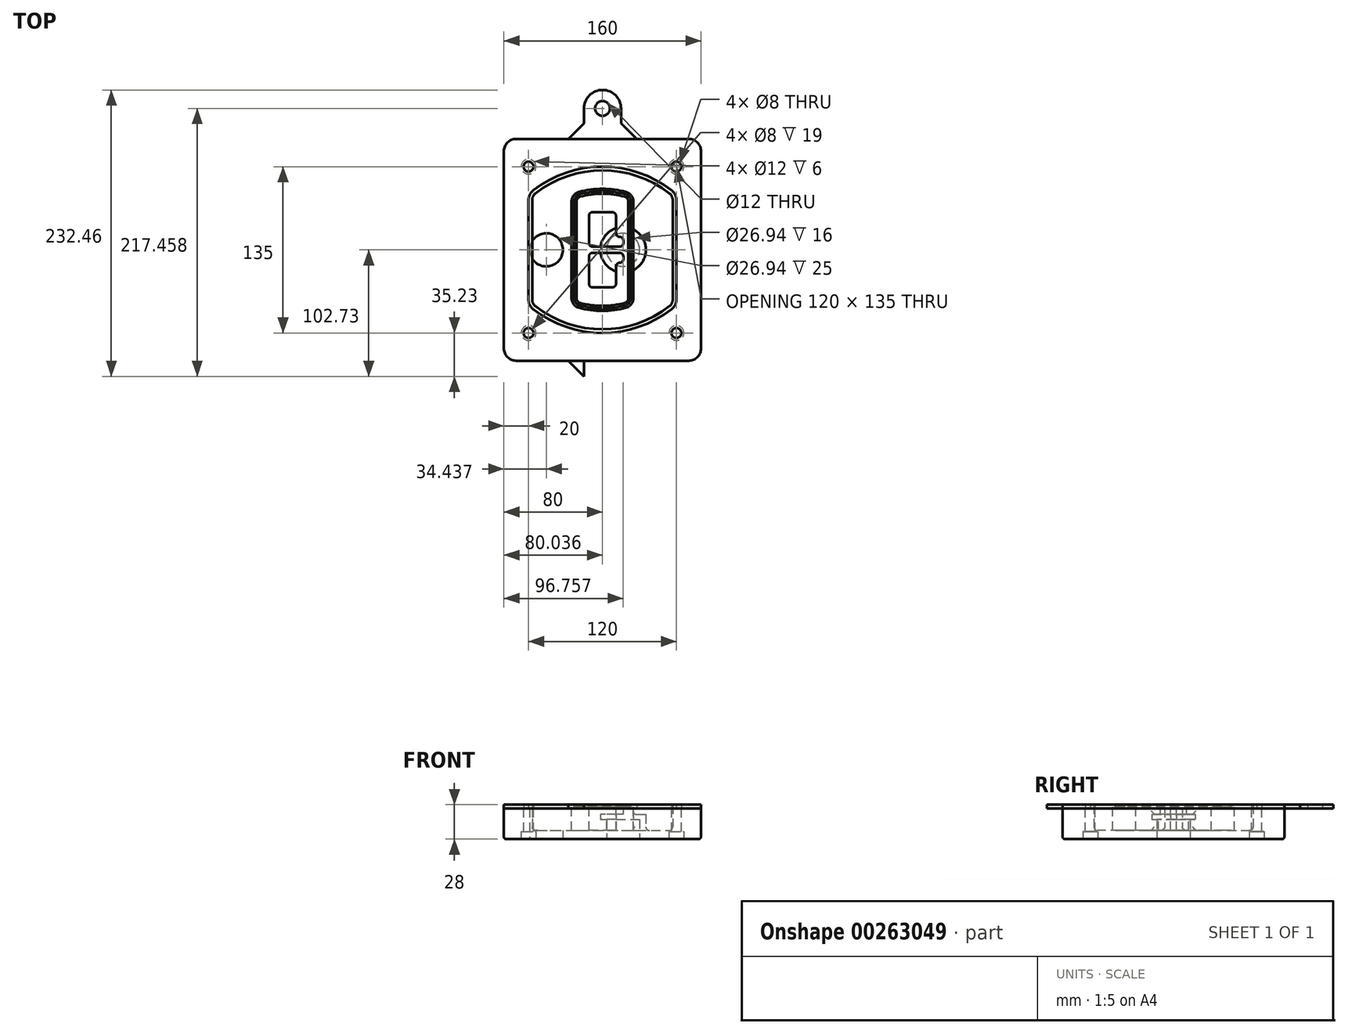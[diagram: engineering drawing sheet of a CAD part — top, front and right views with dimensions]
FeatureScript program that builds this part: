
annotation { "Feature Type Name" : "Feature", "Feature Type Description" : "" }
export const myFeature = defineFeature(function(context is Context, id is Id, definition is map)
    precondition{}
    {
        {
            var Q0;
            Q0=qCreatedBy(makeId("Top.planeOp"),FACE);
            var sketch = newSketch(context, id + "F0", { "sketchPlane" : qUnion([Q0])});
            skPoint(sketch, "E0.rect.middle", {"position": v(0, 0) * mm});
            skLineSegment(sketch, "E1.bottom", {"start": v(-70, -90) * mm, "end": v(70, -90) * mm});
            skLineSegment(sketch, "E1.top", {"start": v(-70, 90) * mm, "end": v(70, 90) * mm});
            skLineSegment(sketch, "E1.left", {"start": v(-80, -80) * mm, "end": v(-80, 80) * mm});
            skLineSegment(sketch, "E1.right", {"start": v(80, -80) * mm, "end": v(80, 80) * mm});
            skLineSegment(sketch, "E2", {"start": v(-80, 90) * mm, "end": v(80, -90) * mm, "construction": true});
            skLineSegment(sketch, "E3", {"start": v(80, 90) * mm, "end": v(-80, -90) * mm, "construction": true});
            skCircle(sketch, "E4", {"center": v(-60, 67.5) * mm, "radius": 4 * mm});
            skCircle(sketch, "E5", {"center": v(60, 67.5) * mm, "radius": 4 * mm});
            skCircle(sketch, "E6", {"center": v(60, -67.5) * mm, "radius": 4 * mm});
            skCircle(sketch, "E7", {"center": v(-60, -67.5) * mm, "radius": 4 * mm});
            skLineSegment(sketch, "E8", {"start": v(-60, 67.5) * mm, "end": v(60, 67.5) * mm, "construction": true});
            skLineSegment(sketch, "E9", {"start": v(60, 67.5) * mm, "end": v(60, -67.5) * mm, "construction": true});
            skLineSegment(sketch, "E10", {"start": v(60, -67.5) * mm, "end": v(-60, -67.5) * mm, "construction": true});
            skLineSegment(sketch, "E11", {"start": v(-60, -67.5) * mm, "end": v(-60, 67.5) * mm, "construction": true});
            skLineSegment(sketch, "E12", {"start": v(-60, 40.3) * mm, "end": v(-60, -40.3) * mm});
            skLineSegment(sketch, "E13", {"start": v(60, 40.3) * mm, "end": v(60, -40.3) * mm});
            skArc(sketch, "E14", {"start": v(56.15, 48.18) * mm, "mid": v(0, 67.5) * mm, "end": v(-56.15, 48.18) * mm});
            skArc(sketch, "E15", {"start": v(-56.15, -48.18) * mm, "mid": v(0, -67.5) * mm, "end": v(56.15, -48.18) * mm});
            skLineSegment(sketch, "E16", {"start": v(-60, 0) * mm, "end": v(60, 0) * mm, "construction": true});
            skPoint(sketch, "E17.visualSharp", {"position": v(-60, -45) * mm});
            skArc(sketch, "E17.filletArc", {"start": v(-60, -40.3) * mm, "mid": v(-58.99, -44.68) * mm, "end": v(-56.15, -48.18) * mm});
            skPoint(sketch, "E18.visualSharp", {"position": v(-60, 45) * mm});
            skArc(sketch, "E18.filletArc", {"start": v(-56.15, 48.18) * mm, "mid": v(-58.99, 44.68) * mm, "end": v(-60, 40.3) * mm});
            skPoint(sketch, "E19.visualSharp", {"position": v(60, 45) * mm});
            skArc(sketch, "E19.filletArc", {"start": v(60, 40.3) * mm, "mid": v(58.99, 44.68) * mm, "end": v(56.15, 48.18) * mm});
            skPoint(sketch, "E20.visualSharp", {"position": v(60, -45) * mm});
            skArc(sketch, "E20.filletArc", {"start": v(56.15, -48.18) * mm, "mid": v(58.99, -44.68) * mm, "end": v(60, -40.3) * mm});
            skPoint(sketch, "E21.visualSharp", {"position": v(-80, 90) * mm});
            skArc(sketch, "E21.filletArc", {"start": v(-70, 90) * mm, "mid": v(-77.07, 87.07) * mm, "end": v(-80, 80) * mm});
            skPoint(sketch, "E22.visualSharp", {"position": v(80, 90) * mm});
            skArc(sketch, "E22.filletArc", {"start": v(80, 80) * mm, "mid": v(77.07, 87.07) * mm, "end": v(70, 90) * mm});
            skPoint(sketch, "E23.visualSharp", {"position": v(80, -90) * mm});
            skArc(sketch, "E23.filletArc", {"start": v(70, -90) * mm, "mid": v(77.07, -87.07) * mm, "end": v(80, -80) * mm});
            skPoint(sketch, "E24.visualSharp", {"position": v(-80, -90) * mm});
            skArc(sketch, "E24.filletArc", {"start": v(-80, -80) * mm, "mid": v(-77.07, -87.07) * mm, "end": v(-70, -90) * mm});
            skArc(sketch, "E25.0", {"start": v(57, 40.3) * mm, "mid": v(56.3, 43.36) * mm, "end": v(54.3, 45.81) * mm});
            skLineSegment(sketch, "E25.1", {"start": v(57, 40.3) * mm, "end": v(57, -40.3) * mm});
            skArc(sketch, "E25.2", {"start": v(54.3, -45.81) * mm, "mid": v(56.3, -43.36) * mm, "end": v(57, -40.3) * mm});
            skArc(sketch, "E25.3", {"start": v(-54.3, -45.81) * mm, "mid": v(0, -64.5) * mm, "end": v(54.3, -45.81) * mm});
            skArc(sketch, "E25.4", {"start": v(-57, -40.3) * mm, "mid": v(-56.3, -43.36) * mm, "end": v(-54.3, -45.81) * mm});
            skArc(sketch, "E25.5", {"start": v(54.3, 45.81) * mm, "mid": v(0, 64.5) * mm, "end": v(-54.3, 45.81) * mm});
            skLineSegment(sketch, "E25.6", {"start": v(-57, 40.3) * mm, "end": v(-57, -40.3) * mm});
            skArc(sketch, "E25.7", {"start": v(-54.3, 45.81) * mm, "mid": v(-56.3, 43.36) * mm, "end": v(-57, 40.3) * mm});
            skArc(sketch, "E26.0", {"start": v(-58.62, 51.33) * mm, "mid": v(-62.58, 46.43) * mm, "end": v(-64, 40.3) * mm});
            skArc(sketch, "E26.1", {"start": v(58.62, 51.33) * mm, "mid": v(0, 71.5) * mm, "end": v(-58.62, 51.33) * mm});
            skArc(sketch, "E26.2", {"start": v(64, 40.3) * mm, "mid": v(62.58, 46.43) * mm, "end": v(58.62, 51.33) * mm});
            skLineSegment(sketch, "E26.3", {"start": v(64, 40.3) * mm, "end": v(64, -40.3) * mm});
            skArc(sketch, "E26.4", {"start": v(58.62, -51.33) * mm, "mid": v(62.58, -46.43) * mm, "end": v(64, -40.3) * mm});
            skLineSegment(sketch, "E26.5", {"start": v(-64, 40.3) * mm, "end": v(-64, -40.3) * mm});
            skArc(sketch, "E26.6", {"start": v(-58.62, -51.33) * mm, "mid": v(0, -71.5) * mm, "end": v(58.62, -51.33) * mm});
            skArc(sketch, "E26.7", {"start": v(-64, -40.3) * mm, "mid": v(-62.58, -46.43) * mm, "end": v(-58.62, -51.33) * mm});
            skSolve(sketch);
        }
        {
            var Q0;
            Q0=makeQuery(id+"F0.imprint","IMPRINT",FACE,{"disambiguationData":[TD([[makeQuery(id+"F0.imprint","IMPRINT",EDGE,{"derivedFrom":sQuery(id+"F0.wireOp",EDGE,"E1.bottom")}),1.0]])]});
            var Q1;
            Q1=makeQuery(id+"F0.imprint","IMPRINT",FACE,{"disambiguationData":[TD([[makeQuery(id+"F0.imprint","IMPRINT",EDGE,{"derivedFrom":sQuery(id+"F0.wireOp",EDGE,"E12")}),1.0]])]});
            var Q2;
            Q2=makeQuery(id+"F0.imprint","IMPRINT",FACE,{"disambiguationData":[TD([[makeQuery(id+"F0.imprint","IMPRINT",EDGE,{"derivedFrom":sQuery(id+"F0.wireOp",EDGE,"E25.0")}),1.0]])]});
            var Q3;
            Q3=makeQuery(id+"F0.imprint","IMPRINT",FACE,{"disambiguationData":[TD([[makeQuery(id+"F0.imprint","IMPRINT",EDGE,{"derivedFrom":sQuery(id+"F0.wireOp",EDGE,"E12")}),-1.0]])]});
            extrude(context, id + "F1", {"entities" : qUnion([Q0, Q1, Q2, Q3]), "oppositeDirection" : true, "depth" : 25 * mm});
        }
        {
            var Q0;
            Q0=makeQuery(id+"F0.imprint","IMPRINT",FACE,{"disambiguationData":[TD([[makeQuery(id+"F0.imprint","IMPRINT",EDGE,{"derivedFrom":sQuery(id+"F0.wireOp",EDGE,"E12")}),1.0]])]});
            extrude(context, id + "F2", {"entities" : qUnion([Q0]), "operationType" : NewBodyOperationType.ADD, "depth" : 3 * mm});
        }
        {
            var Q0;
            Q0=makeQuery(id+"F0.imprint","IMPRINT",FACE,{"disambiguationData":[TD([[makeQuery(id+"F0.imprint","IMPRINT",EDGE,{"derivedFrom":sQuery(id+"F0.wireOp",EDGE,"E25.0")}),1.0]])]});
            extrude(context, id + "F3", {"entities" : qUnion([Q0]), "operationType" : NewBodyOperationType.REMOVE, "oppositeDirection" : true, "depth" : 18 * mm});
        }
        {
            var Q0;
            Q0=makeQuery(id+"F2.opExtrude","CAP_FACE",FACE,{"disambiguationData":[OSD([sQuery(id+"F0.wireOp",EDGE,"E12"),sQuery(id+"F0.wireOp",EDGE,"E13"),sQuery(id+"F0.wireOp",EDGE,"E14"),sQuery(id+"F0.wireOp",EDGE,"E15"),sQuery(id+"F0.wireOp",EDGE,"E17.filletArc"),sQuery(id+"F0.wireOp",EDGE,"E18.filletArc"),sQuery(id+"F0.wireOp",EDGE,"E19.filletArc"),sQuery(id+"F0.wireOp",EDGE,"E20.filletArc"),sQuery(id+"F0.wireOp",EDGE,"E25.0"),sQuery(id+"F0.wireOp",EDGE,"E25.1"),sQuery(id+"F0.wireOp",EDGE,"E25.2"),sQuery(id+"F0.wireOp",EDGE,"E25.3"),sQuery(id+"F0.wireOp",EDGE,"E25.4"),sQuery(id+"F0.wireOp",EDGE,"E25.5"),sQuery(id+"F0.wireOp",EDGE,"E25.6"),sQuery(id+"F0.wireOp",EDGE,"E25.7")])],"isStart":false});
            var sketch = newSketch(context, id + "F4", { "sketchPlane" : qUnion([Q0])});
            skArc(sketch, "E27.0", {"start": v(-19.08, -46.97) * mm, "mid": v(0, -49.5) * mm, "end": v(19.08, -46.97) * mm});
            skArc(sketch, "E28.0", {"start": v(19.08, 46.97) * mm, "mid": v(0, 49.5) * mm, "end": v(-19.08, 46.97) * mm});
            skLineSegment(sketch, "E29", {"start": v(-25, 39.25) * mm, "end": v(-25, -39.25) * mm});
            skLineSegment(sketch, "E30", {"start": v(25, 39.25) * mm, "end": v(25, -39.25) * mm});
            skLineSegment(sketch, "E31", {"start": v(-25, 45.1) * mm, "end": v(25, 45.1) * mm, "construction": true});
            skLineSegment(sketch, "E32", {"start": v(-25, -45.1) * mm, "end": v(25, -45.1) * mm, "construction": true});
            skPoint(sketch, "E33.visualSharp", {"position": v(-25, 45.1) * mm});
            skArc(sketch, "E33.filletArc", {"start": v(-19.08, 46.97) * mm, "mid": v(-23.35, 44.11) * mm, "end": v(-25, 39.25) * mm});
            skPoint(sketch, "E34.visualSharp", {"position": v(25, 45.1) * mm});
            skArc(sketch, "E34.filletArc", {"start": v(25, 39.25) * mm, "mid": v(23.35, 44.11) * mm, "end": v(19.08, 46.97) * mm});
            skPoint(sketch, "E35.visualSharp", {"position": v(25, -45.1) * mm});
            skArc(sketch, "E35.filletArc", {"start": v(19.08, -46.97) * mm, "mid": v(23.35, -44.11) * mm, "end": v(25, -39.25) * mm});
            skPoint(sketch, "E36.visualSharp", {"position": v(-25, -45.1) * mm});
            skArc(sketch, "E36.filletArc", {"start": v(-25, -39.25) * mm, "mid": v(-23.35, -44.11) * mm, "end": v(-19.08, -46.97) * mm});
            skArc(sketch, "E37.0", {"start": v(54.3, 45.81) * mm, "mid": v(0, 64.5) * mm, "end": v(-54.3, 45.81) * mm});
            skArc(sketch, "E37.1", {"start": v(-54.3, 45.81) * mm, "mid": v(-56.3, 43.36) * mm, "end": v(-57, 40.3) * mm});
            skLineSegment(sketch, "E37.2", {"start": v(-57, 40.3) * mm, "end": v(-57, -40.3) * mm});
            skArc(sketch, "E37.3", {"start": v(-57, -40.3) * mm, "mid": v(-56.3, -43.36) * mm, "end": v(-54.3, -45.81) * mm});
            skArc(sketch, "E37.4", {"start": v(-54.3, -45.81) * mm, "mid": v(0, -64.5) * mm, "end": v(54.3, -45.81) * mm});
            skArc(sketch, "E37.5", {"start": v(54.3, -45.81) * mm, "mid": v(56.3, -43.36) * mm, "end": v(57, -40.3) * mm});
            skLineSegment(sketch, "E37.6", {"start": v(57, 40.3) * mm, "end": v(57, -40.3) * mm});
            skArc(sketch, "E37.7", {"start": v(57, 40.3) * mm, "mid": v(56.3, 43.36) * mm, "end": v(54.3, 45.81) * mm});
            skLineSegment(sketch, "E38.0", {"start": v(23, 39.25) * mm, "end": v(23, -39.25) * mm});
            skArc(sketch, "E38.1", {"start": v(18.56, -45.04) * mm, "mid": v(21.76, -42.9) * mm, "end": v(23, -39.25) * mm});
            skArc(sketch, "E38.2", {"start": v(-18.56, -45.04) * mm, "mid": v(0, -47.5) * mm, "end": v(18.56, -45.04) * mm});
            skArc(sketch, "E38.3", {"start": v(-23, -39.25) * mm, "mid": v(-21.76, -42.9) * mm, "end": v(-18.56, -45.04) * mm});
            skLineSegment(sketch, "E38.4", {"start": v(-23, 39.25) * mm, "end": v(-23, -39.25) * mm});
            skArc(sketch, "E38.5", {"start": v(23, 39.25) * mm, "mid": v(21.76, 42.9) * mm, "end": v(18.56, 45.04) * mm});
            skArc(sketch, "E38.6", {"start": v(-18.56, 45.04) * mm, "mid": v(-21.76, 42.9) * mm, "end": v(-23, 39.25) * mm});
            skArc(sketch, "E38.7", {"start": v(18.56, 45.04) * mm, "mid": v(0, 47.5) * mm, "end": v(-18.56, 45.04) * mm});
            skArc(sketch, "E39.0", {"start": v(21, 39.25) * mm, "mid": v(20.18, 41.68) * mm, "end": v(18.04, 43.1) * mm});
            skLineSegment(sketch, "E39.1", {"start": v(21, 39.25) * mm, "end": v(21, -39.25) * mm});
            skArc(sketch, "E39.2", {"start": v(18.04, -43.1) * mm, "mid": v(20.18, -41.68) * mm, "end": v(21, -39.25) * mm});
            skArc(sketch, "E39.3", {"start": v(-18.04, -43.1) * mm, "mid": v(0, -45.5) * mm, "end": v(18.04, -43.1) * mm});
            skArc(sketch, "E39.4", {"start": v(-21, -39.25) * mm, "mid": v(-20.18, -41.68) * mm, "end": v(-18.04, -43.1) * mm});
            skArc(sketch, "E39.5", {"start": v(18.04, 43.1) * mm, "mid": v(0, 45.5) * mm, "end": v(-18.04, 43.1) * mm});
            skLineSegment(sketch, "E39.6", {"start": v(-21, 39.25) * mm, "end": v(-21, -39.25) * mm});
            skArc(sketch, "E39.7", {"start": v(-18.04, 43.1) * mm, "mid": v(-20.18, 41.68) * mm, "end": v(-21, 39.25) * mm});
            skLineSegment(sketch, "E40", {"start": v(-25, 0) * mm, "end": v(25, 0) * mm, "construction": true});
            skLineSegment(sketch, "E41", {"start": v(-11, 5.5) * mm, "end": v(-11, 27.5) * mm});
            skLineSegment(sketch, "E42", {"start": v(-8, 30.5) * mm, "end": v(8, 30.5) * mm});
            skLineSegment(sketch, "E43", {"start": v(11, 27.5) * mm, "end": v(11, 13.5) * mm});
            skLineSegment(sketch, "E44", {"start": v(14, 10.5) * mm, "end": v(14, 10.5) * mm});
            skLineSegment(sketch, "E45", {"start": v(17, 7.5) * mm, "end": v(17, 5.5) * mm});
            skLineSegment(sketch, "E46", {"start": v(14, 2.5) * mm, "end": v(-8, 2.5) * mm});
            skPoint(sketch, "E47.visualSharp", {"position": v(-11, 30.5) * mm});
            skArc(sketch, "E47.filletArc", {"start": v(-8, 30.5) * mm, "mid": v(-10.12, 29.62) * mm, "end": v(-11, 27.5) * mm});
            skPoint(sketch, "E48.visualSharp", {"position": v(11, 30.5) * mm});
            skArc(sketch, "E48.filletArc", {"start": v(11, 27.5) * mm, "mid": v(10.12, 29.62) * mm, "end": v(8, 30.5) * mm});
            skPoint(sketch, "E49.visualSharp", {"position": v(11, 10.5) * mm});
            skArc(sketch, "E49.filletArc", {"start": v(11, 13.5) * mm, "mid": v(11.88, 11.38) * mm, "end": v(14, 10.5) * mm});
            skPoint(sketch, "E50.visualSharp", {"position": v(17, 10.5) * mm});
            skArc(sketch, "E50.filletArc", {"start": v(17, 7.5) * mm, "mid": v(16.12, 9.62) * mm, "end": v(14, 10.5) * mm});
            skPoint(sketch, "E51.visualSharp", {"position": v(17, 2.5) * mm});
            skArc(sketch, "E51.filletArc", {"start": v(14, 2.5) * mm, "mid": v(16.12, 3.38) * mm, "end": v(17, 5.5) * mm});
            skPoint(sketch, "E52.visualSharp", {"position": v(-11, 2.5) * mm});
            skArc(sketch, "E52.filletArc", {"start": v(-11, 5.5) * mm, "mid": v(-10.12, 3.38) * mm, "end": v(-8, 2.5) * mm});
            skLineSegment(sketch, "E53.0.MirrorCS", {"start": v(14, -2.5) * mm, "end": v(-8, -2.5) * mm});
            skArc(sketch, "E54.0.MirrorCS", {"start": v(-11, -5.5) * mm, "mid": v(-10.12, -3.38) * mm, "end": v(-8, -2.5) * mm});
            skLineSegment(sketch, "E55.0.MirrorCS", {"start": v(-11, -5.5) * mm, "end": v(-11, -27.5) * mm});
            skArc(sketch, "E56.0.MirrorCS", {"start": v(-8, -30.5) * mm, "mid": v(-10.12, -29.62) * mm, "end": v(-11, -27.5) * mm});
            skLineSegment(sketch, "E57.0.MirrorCS", {"start": v(-8, -30.5) * mm, "end": v(8, -30.5) * mm});
            skArc(sketch, "E58.0.MirrorCS", {"start": v(11, -27.5) * mm, "mid": v(10.12, -29.62) * mm, "end": v(8, -30.5) * mm});
            skLineSegment(sketch, "E59.0.MirrorCS", {"start": v(11, -27.5) * mm, "end": v(11, -13.5) * mm});
            skArc(sketch, "E60.0.MirrorCS", {"start": v(11, -13.5) * mm, "mid": v(11.88, -11.38) * mm, "end": v(14, -10.5) * mm});
            skArc(sketch, "E61.0.MirrorCS", {"start": v(17, -7.5) * mm, "mid": v(16.12, -9.62) * mm, "end": v(14, -10.5) * mm});
            skLineSegment(sketch, "E62.0.MirrorCS", {"start": v(17, -7.5) * mm, "end": v(17, -5.5) * mm});
            skArc(sketch, "E63.0.MirrorCS", {"start": v(14, -2.5) * mm, "mid": v(16.12, -3.38) * mm, "end": v(17, -5.5) * mm});
            skSolve(sketch);
        }
        {
            var Q0;
            Q0=makeQuery(id+"F4.imprint","IMPRINT",FACE,{"disambiguationData":[TD([[makeQuery(id+"F4.imprint","IMPRINT",EDGE,{"derivedFrom":sQuery(id+"F4.wireOp",EDGE,"E27.0")}),1.0]])]});
            var Q1;
            Q1=makeQuery(id+"F4.imprint","IMPRINT",FACE,{"disambiguationData":[TD([[makeQuery(id+"F4.imprint","IMPRINT",EDGE,{"derivedFrom":sQuery(id+"F4.wireOp",EDGE,"E38.0")}),-1.0]])]});
            var Q2;
            Q2=makeQuery(id+"F4.imprint","IMPRINT",FACE,{"disambiguationData":[TD([[makeQuery(id+"F4.imprint","IMPRINT",EDGE,{"derivedFrom":sQuery(id+"F4.wireOp",EDGE,"E39.0")}),1.0]])]});
            extrude(context, id + "F5", {"entities" : qUnion([Q0, Q1, Q2]), "operationType" : NewBodyOperationType.ADD, "endBound" : BoundingType.UP_TO_NEXT, "oppositeDirection" : true, "depth" : 25 * mm});
        }
        {
            var Q0;
            Q0=makeQuery(id+"F4.imprint","IMPRINT",FACE,{"disambiguationData":[TD([[makeQuery(id+"F4.imprint","IMPRINT",EDGE,{"derivedFrom":sQuery(id+"F4.wireOp",EDGE,"E38.0")}),-1.0]])]});
            extrude(context, id + "F6", {"entities" : qUnion([Q0]), "operationType" : NewBodyOperationType.REMOVE, "oppositeDirection" : true, "depth" : 2 * mm});
        }
        {
            var Q0;
            Q0=makeQuery(id+"F1.opExtrude","CAP_FACE",FACE,{"disambiguationData":[OSD([sQuery(id+"F0.wireOp",EDGE,"E1.bottom"),sQuery(id+"F0.wireOp",EDGE,"E1.top"),sQuery(id+"F0.wireOp",EDGE,"E1.left"),sQuery(id+"F0.wireOp",EDGE,"E1.right"),sQuery(id+"F0.wireOp",EDGE,"E4"),sQuery(id+"F0.wireOp",EDGE,"E5"),sQuery(id+"F0.wireOp",EDGE,"E6"),sQuery(id+"F0.wireOp",EDGE,"E7"),sQuery(id+"F0.wireOp",EDGE,"E21.filletArc"),sQuery(id+"F0.wireOp",EDGE,"E22.filletArc"),sQuery(id+"F0.wireOp",EDGE,"E23.filletArc"),sQuery(id+"F0.wireOp",EDGE,"E24.filletArc")])],"isStart":false});
            var sketch = newSketch(context, id + "F7", { "sketchPlane" : qUnion([Q0])});
            skCircle(sketch, "E64", {"center": v(16.76, 0) * mm, "radius": 13.47 * mm});
            skCircle(sketch, "E65", {"center": v(-45.56, 0) * mm, "radius": 13.47 * mm});
            skLineSegment(sketch, "E66", {"start": v(80, 0) * mm, "end": v(-80, 0) * mm});
            skCircle(sketch, "E67", {"center": v(16.76, 0) * mm, "radius": 18.47 * mm});
            skCircle(sketch, "E68", {"center": v(60, -67.5) * mm, "radius": 6 * mm});
            skCircle(sketch, "E69", {"center": v(-60, -67.5) * mm, "radius": 6 * mm});
            skCircle(sketch, "E70", {"center": v(-60, 67.5) * mm, "radius": 6 * mm});
            skCircle(sketch, "E71", {"center": v(60, 67.5) * mm, "radius": 6 * mm});
            skSolve(sketch);
        }
        {
            var Q0;
            {var subQ1=sQuery(id+"F7.wireOp",EDGE,"E66");var subQ4=sQuery(id+"F7.wireOp",EDGE,"E64");var subQ6=makeQuery(id+"F7.imprint","INTERSECT",VERTEX,{"disambiguationData":[OD(0.0)],"derivedFrom":[subQ4,subQ1]});Q0=makeQuery(id+"F7.imprint","IMPRINT",FACE,{"disambiguationData":[TD([[makeQuery(id+"F7.imprint","IMPRINT",EDGE,{"disambiguationData":[TD([[subQ6,-1.0]])],"derivedFrom":subQ4}),-1.0]])]});}
            var Q1;
            {var subQ0=sQuery(id+"F7.wireOp",EDGE,"E66");var subQ1=sQuery(id+"F7.wireOp",EDGE,"E64");var subQ3=makeQuery(id+"F7.imprint","INTERSECT",VERTEX,{"disambiguationData":[OD(0.0)],"derivedFrom":[subQ1,subQ0]});Q1=makeQuery(id+"F7.imprint","IMPRINT",FACE,{"disambiguationData":[TD([[makeQuery(id+"F7.imprint","IMPRINT",EDGE,{"disambiguationData":[TD([[subQ3,-1.0]])],"derivedFrom":subQ1}),1.0]])]});}
            var Q2;
            {var subQ0=sQuery(id+"F7.wireOp",EDGE,"E66");var subQ1=sQuery(id+"F7.wireOp",EDGE,"E64");var subQ3=makeQuery(id+"F7.imprint","INTERSECT",VERTEX,{"disambiguationData":[OD(0.0)],"derivedFrom":[subQ1,subQ0]});Q2=makeQuery(id+"F7.imprint","IMPRINT",FACE,{"disambiguationData":[TD([[makeQuery(id+"F7.imprint","IMPRINT",EDGE,{"disambiguationData":[TD([[subQ3,1.0]])],"derivedFrom":subQ1}),1.0]])]});}
            var Q3;
            {var subQ1=sQuery(id+"F7.wireOp",EDGE,"E66");var subQ4=sQuery(id+"F7.wireOp",EDGE,"E64");var subQ6=makeQuery(id+"F7.imprint","INTERSECT",VERTEX,{"disambiguationData":[OD(0.0)],"derivedFrom":[subQ4,subQ1]});Q3=makeQuery(id+"F7.imprint","IMPRINT",FACE,{"disambiguationData":[TD([[makeQuery(id+"F7.imprint","IMPRINT",EDGE,{"disambiguationData":[TD([[subQ6,1.0]])],"derivedFrom":subQ4}),-1.0]])]});}
            extrude(context, id + "F8", {"entities" : qUnion([Q0, Q1, Q2, Q3]), "operationType" : NewBodyOperationType.ADD, "oppositeDirection" : true, "depth" : 20 * mm});
        }
        {
            var Q0;
            {var subQ0=sQuery(id+"F7.wireOp",EDGE,"E66");var subQ1=sQuery(id+"F7.wireOp",EDGE,"E64");var subQ3=makeQuery(id+"F7.imprint","INTERSECT",VERTEX,{"disambiguationData":[OD(0.0)],"derivedFrom":[subQ1,subQ0]});Q0=makeQuery(id+"F7.imprint","IMPRINT",FACE,{"disambiguationData":[TD([[makeQuery(id+"F7.imprint","IMPRINT",EDGE,{"disambiguationData":[TD([[subQ3,-1.0]])],"derivedFrom":subQ1}),1.0]])]});}
            var Q1;
            {var subQ0=sQuery(id+"F7.wireOp",EDGE,"E66");var subQ1=sQuery(id+"F7.wireOp",EDGE,"E64");var subQ3=makeQuery(id+"F7.imprint","INTERSECT",VERTEX,{"disambiguationData":[OD(0.0)],"derivedFrom":[subQ1,subQ0]});Q1=makeQuery(id+"F7.imprint","IMPRINT",FACE,{"disambiguationData":[TD([[makeQuery(id+"F7.imprint","IMPRINT",EDGE,{"disambiguationData":[TD([[subQ3,1.0]])],"derivedFrom":subQ1}),1.0]])]});}
            extrude(context, id + "F9", {"entities" : qUnion([Q0, Q1]), "operationType" : NewBodyOperationType.REMOVE, "oppositeDirection" : true, "depth" : 16 * mm});
        }
        {
            var Q0;
            {var subQ0=sQuery(id+"F7.wireOp",EDGE,"E66");var subQ1=sQuery(id+"F7.wireOp",EDGE,"E65");var subQ3=makeQuery(id+"F7.imprint","INTERSECT",VERTEX,{"disambiguationData":[OD(0.0)],"derivedFrom":[subQ1,subQ0]});Q0=makeQuery(id+"F7.imprint","IMPRINT",FACE,{"disambiguationData":[TD([[makeQuery(id+"F7.imprint","IMPRINT",EDGE,{"disambiguationData":[TD([[subQ3,-1.0]])],"derivedFrom":subQ1}),1.0]])]});}
            var Q1;
            {var subQ0=sQuery(id+"F7.wireOp",EDGE,"E66");var subQ1=sQuery(id+"F7.wireOp",EDGE,"E65");var subQ3=makeQuery(id+"F7.imprint","INTERSECT",VERTEX,{"disambiguationData":[OD(0.0)],"derivedFrom":[subQ1,subQ0]});Q1=makeQuery(id+"F7.imprint","IMPRINT",FACE,{"disambiguationData":[TD([[makeQuery(id+"F7.imprint","IMPRINT",EDGE,{"disambiguationData":[TD([[subQ3,1.0]])],"derivedFrom":subQ1}),1.0]])]});}
            extrude(context, id + "F10", {"entities" : qUnion([Q0, Q1]), "operationType" : NewBodyOperationType.REMOVE, "oppositeDirection" : true, "depth" : 25 * mm});
        }
        {
            var Q0;
            Q0=makeQuery(id+"F7.imprint","IMPRINT",FACE,{"disambiguationData":[TD([[makeQuery(id+"F7.imprint","IMPRINT",EDGE,{"derivedFrom":sQuery(id+"F7.wireOp",EDGE,"E68")}),1.0]])]});
            var Q1;
            Q1=makeQuery(id+"F7.imprint","IMPRINT",FACE,{"disambiguationData":[TD([[makeQuery(id+"F7.imprint","IMPRINT",EDGE,{"derivedFrom":makeQuery(id+"F1.opExtrude","CAP_EDGE",EDGE,{"disambiguationData":[OSD([sQuery(id+"F0.wireOp",EDGE,"E5")])],"isStart":false})}),-1.0]])]});
            var Q2;
            Q2=makeQuery(id+"F7.imprint","IMPRINT",FACE,{"disambiguationData":[TD([[makeQuery(id+"F7.imprint","IMPRINT",EDGE,{"derivedFrom":sQuery(id+"F7.wireOp",EDGE,"E69")}),1.0]])]});
            var Q3;
            Q3=makeQuery(id+"F7.imprint","IMPRINT",FACE,{"disambiguationData":[TD([[makeQuery(id+"F7.imprint","IMPRINT",EDGE,{"derivedFrom":makeQuery(id+"F1.opExtrude","CAP_EDGE",EDGE,{"disambiguationData":[OSD([sQuery(id+"F0.wireOp",EDGE,"E4")])],"isStart":false})}),-1.0]])]});
            var Q4;
            Q4=makeQuery(id+"F7.imprint","IMPRINT",FACE,{"disambiguationData":[TD([[makeQuery(id+"F7.imprint","IMPRINT",EDGE,{"derivedFrom":sQuery(id+"F7.wireOp",EDGE,"E70")}),1.0]])]});
            var Q5;
            Q5=makeQuery(id+"F7.imprint","IMPRINT",FACE,{"disambiguationData":[TD([[makeQuery(id+"F7.imprint","IMPRINT",EDGE,{"derivedFrom":makeQuery(id+"F1.opExtrude","CAP_EDGE",EDGE,{"disambiguationData":[OSD([sQuery(id+"F0.wireOp",EDGE,"E7")])],"isStart":false})}),-1.0]])]});
            var Q6;
            Q6=makeQuery(id+"F7.imprint","IMPRINT",FACE,{"disambiguationData":[TD([[makeQuery(id+"F7.imprint","IMPRINT",EDGE,{"derivedFrom":sQuery(id+"F7.wireOp",EDGE,"E71")}),1.0]])]});
            var Q7;
            Q7=makeQuery(id+"F7.imprint","IMPRINT",FACE,{"disambiguationData":[TD([[makeQuery(id+"F7.imprint","IMPRINT",EDGE,{"derivedFrom":makeQuery(id+"F1.opExtrude","CAP_EDGE",EDGE,{"disambiguationData":[OSD([sQuery(id+"F0.wireOp",EDGE,"E6")])],"isStart":false})}),-1.0]])]});
            extrude(context, id + "F11", {"entities" : qUnion([Q0, Q1, Q2, Q3, Q4, Q5, Q6, Q7]), "operationType" : NewBodyOperationType.REMOVE, "oppositeDirection" : true, "depth" : 6 * mm});
        }
        {
            var Q0;
            Q0=makeQuery(id+"F9.boolean.opBoolean","COPY",FACE,{"derivedFrom":makeQuery(id+"F9.opExtrude","CAP_FACE",FACE,{"disambiguationData":[OSD([sQuery(id+"F7.wireOp",EDGE,"E64")])],"isStart":false})});
            var sketch = newSketch(context, id + "F12", { "sketchPlane" : qUnion([Q0])});
            skArc(sketch, "E72.0", {"start": v(11, 17.55) * mm, "mid": v(2.57, 11.82) * mm, "end": v(-1.54, 2.5) * mm});
            skArc(sketch, "E72.1", {"start": v(-1.54, -2.5) * mm, "mid": v(2.57, -11.82) * mm, "end": v(11, -17.55) * mm});
            skLineSegment(sketch, "E73", {"start": v(-1.54, -2.5) * mm, "end": v(14, -2.5) * mm});
            skLineSegment(sketch, "E74.0", {"start": v(14, 2.5) * mm, "end": v(-1.54, 2.5) * mm});
            skArc(sketch, "E74.1", {"start": v(14, 2.5) * mm, "mid": v(16.12, 3.38) * mm, "end": v(17, 5.5) * mm});
            skLineSegment(sketch, "E74.2", {"start": v(17, 7.5) * mm, "end": v(17, 5.5) * mm});
            skArc(sketch, "E74.3", {"start": v(17, 7.5) * mm, "mid": v(16.12, 9.62) * mm, "end": v(14, 10.5) * mm});
            skArc(sketch, "E74.4", {"start": v(11, 13.5) * mm, "mid": v(11.88, 11.38) * mm, "end": v(14, 10.5) * mm});
            skLineSegment(sketch, "E74.5", {"start": v(11, 17.55) * mm, "end": v(11, 13.5) * mm});
            skLineSegment(sketch, "E74.7", {"start": v(14, -2.5) * mm, "end": v(-1.54, -2.5) * mm});
            skArc(sketch, "E74.8", {"start": v(14, -2.5) * mm, "mid": v(16.12, -3.38) * mm, "end": v(17, -5.5) * mm});
            skLineSegment(sketch, "E74.9", {"start": v(17, -7.5) * mm, "end": v(17, -5.5) * mm});
            skArc(sketch, "E74.10", {"start": v(17, -7.5) * mm, "mid": v(16.12, -9.62) * mm, "end": v(14, -10.5) * mm});
            skArc(sketch, "E74.11", {"start": v(11, -13.5) * mm, "mid": v(11.88, -11.38) * mm, "end": v(14, -10.5) * mm});
            skLineSegment(sketch, "E74.12", {"start": v(11, -17.55) * mm, "end": v(11, -13.5) * mm});
            skPoint(sketch, "E75.orphan", {"position": v(11, -27.5) * mm});
            skPoint(sketch, "E76.orphan", {"position": v(-8, -2.5) * mm});
            skPoint(sketch, "E77.orphan", {"position": v(-8, 2.5) * mm});
            skPoint(sketch, "E78.orphan", {"position": v(11, 27.5) * mm});
            skSolve(sketch);
        }
        {
            var Q0;
            {var subQ7=sQuery(id+"F12.wireOp",EDGE,"E72.0");var subQ14=sQuery(id+"F12.wireOp",EDGE,"E72.1");var subQ16=sQuery(id+"F12.wireOp",EDGE,"E74.1");var subQ18=sQuery(id+"F12.wireOp",EDGE,"E74.8");Q0=qUnion([makeQuery(id+"F12.imprint","IMPRINT",FACE,{"disambiguationData":[TD([[makeQuery(id+"F12.imprint","IMPRINT",EDGE,{"derivedFrom":subQ7}),1.0]])]}),makeQuery(id+"F12.imprint","IMPRINT",FACE,{"disambiguationData":[TD([[makeQuery(id+"F12.imprint","IMPRINT",EDGE,{"derivedFrom":subQ14}),1.0]])]}),makeQuery(id+"F12.imprint","IMPRINT",FACE,{"disambiguationData":[TD([[makeQuery(id+"F12.imprint","IMPRINT",EDGE,{"derivedFrom":subQ16}),1.0]])]}),makeQuery(id+"F12.imprint","IMPRINT",FACE,{"disambiguationData":[TD([[makeQuery(id+"F12.imprint","IMPRINT",EDGE,{"derivedFrom":subQ18}),-1.0]])]})]);}
            var Q1;
            Q1=makeQuery(id+"F5.boolean.opBoolean","SPLIT",FACE,{"disambiguationData":[TD([makeQuery(id+"F5.opExtrude","SWEPT_FACE",FACE,{"disambiguationData":[OSD([sQuery(id+"F4.wireOp",EDGE,"E41")])]})])],"derivedFrom":makeQuery(id+"F3.boolean.opBoolean","COPY",FACE,{"derivedFrom":makeQuery(id+"F3.opExtrude","CAP_FACE",FACE,{"disambiguationData":[OSD([sQuery(id+"F0.wireOp",EDGE,"E25.0"),sQuery(id+"F0.wireOp",EDGE,"E25.1"),sQuery(id+"F0.wireOp",EDGE,"E25.2"),sQuery(id+"F0.wireOp",EDGE,"E25.3"),sQuery(id+"F0.wireOp",EDGE,"E25.4"),sQuery(id+"F0.wireOp",EDGE,"E25.5"),sQuery(id+"F0.wireOp",EDGE,"E25.6"),sQuery(id+"F0.wireOp",EDGE,"E25.7")])],"isStart":false})})});
            extrude(context, id + "F13", {"entities" : qUnion([Q0]), "operationType" : NewBodyOperationType.REMOVE, "endBound" : BoundingType.UP_TO_SURFACE, "endBoundEntityFace" : qUnion([Q1]), "depth" : 25 * mm});
        }
        {
            var Q0;
            Q0=makeQuery(id+"F3.boolean.opBoolean","COPY",EDGE,{"derivedFrom":makeQuery(id+"F3.opExtrude","CAP_EDGE",EDGE,{"disambiguationData":[OSD([sQuery(id+"F0.wireOp",EDGE,"E25.6")])],"isStart":false})});
            var Q1;
            Q1=makeQuery(id+"F8.boolean.opBoolean","INTERSECT",EDGE,{"derivedFrom":[makeQuery(id+"F5.opExtrude","SWEPT_FACE",FACE,{"disambiguationData":[OSD([sQuery(id+"F4.wireOp",EDGE,"E30")])]}),makeQuery(id+"F8.opExtrude","CAP_FACE",FACE,{"disambiguationData":[OSD([sQuery(id+"F7.wireOp",EDGE,"E67")])],"isStart":false})]});
            var Q2;
            Q2=makeQuery(id+"F8.boolean.opBoolean","INTERSECT",EDGE,{"disambiguationData":[OD(1.0)],"derivedFrom":[makeQuery(id+"F5.opExtrude","SWEPT_FACE",FACE,{"disambiguationData":[OSD([sQuery(id+"F4.wireOp",EDGE,"E30")])]}),makeQuery(id+"F8.opExtrude","SWEPT_FACE",FACE,{"disambiguationData":[OSD([sQuery(id+"F7.wireOp",EDGE,"E67")])]})]});
            var Q3;
            {var subQ0=sQuery(id+"F4.wireOp",EDGE,"E30");Q3=makeQuery(id+"F8.boolean.opBoolean","SPLIT",EDGE,{"disambiguationData":[TD([makeQuery(id+"F5.opExtrude","SWEPT_FACE",FACE,{"disambiguationData":[OSD([sQuery(id+"F4.wireOp",EDGE,"E35.filletArc")])]})])],"derivedFrom":makeQuery(id+"F5.opExtrude","CAP_EDGE",EDGE,{"disambiguationData":[OSD([subQ0])],"isStart":false})});}
            var Q4;
            {var subQ0=sQuery(id+"F0.wireOp",EDGE,"E25.7");var subQ1=sQuery(id+"F0.wireOp",EDGE,"E25.1");var subQ2=sQuery(id+"F0.wireOp",EDGE,"E25.6");var subQ3=sQuery(id+"F0.wireOp",EDGE,"E25.5");var subQ4=sQuery(id+"F0.wireOp",EDGE,"E25.4");var subQ5=sQuery(id+"F0.wireOp",EDGE,"E25.0");var subQ6=sQuery(id+"F0.wireOp",EDGE,"E25.2");var subQ7=sQuery(id+"F0.wireOp",EDGE,"E25.3");Q4=makeQuery(id+"F8.boolean.opBoolean","INTERSECT",EDGE,{"derivedFrom":[makeQuery(id+"F5.boolean.opBoolean","SPLIT",FACE,{"disambiguationData":[TD([makeQuery(id+"F2.opExtrude","SWEPT_FACE",FACE,{"disambiguationData":[OSD([subQ5])]})])],"derivedFrom":makeQuery(id+"F3.boolean.opBoolean","COPY",FACE,{"derivedFrom":makeQuery(id+"F3.opExtrude","CAP_FACE",FACE,{"disambiguationData":[OSD([subQ5,subQ1,subQ6,subQ7,subQ4,subQ3,subQ2,subQ0])],"isStart":false})})}),makeQuery(id+"F8.opExtrude","SWEPT_FACE",FACE,{"disambiguationData":[OSD([sQuery(id+"F7.wireOp",EDGE,"E67")])]})]});}
            var Q5;
            Q5=makeQuery(id+"F8.boolean.opBoolean","INTERSECT",EDGE,{"disambiguationData":[OD(0.0)],"derivedFrom":[makeQuery(id+"F5.opExtrude","SWEPT_FACE",FACE,{"disambiguationData":[OSD([sQuery(id+"F4.wireOp",EDGE,"E30")])]}),makeQuery(id+"F8.opExtrude","SWEPT_FACE",FACE,{"disambiguationData":[OSD([sQuery(id+"F7.wireOp",EDGE,"E67")])]})]});
            fillet(context, id + "F14", {"entities" : qUnion([Q0, Q1, Q2, Q3, Q4, Q5]), "radius" : 3 * mm, "tangentPropagation" : true, "allowEdgeOverflow" : false});
        }
        {
            var Q0;
            Q0=makeQuery(id+"F1.opExtrude","CAP_EDGE",EDGE,{"disambiguationData":[OSD([sQuery(id+"F0.wireOp",EDGE,"E1.bottom")])],"isStart":false});
            fillet(context, id + "F15", {"entities" : qUnion([Q0]), "radius" : 2 * mm, "tangentPropagation" : true, "allowEdgeOverflow" : false});
        }
        {
            var Q0;
            Q0=qCreatedBy(makeId("Top.planeOp"),FACE);
            var sketch = newSketch(context, id + "F16", { "sketchPlane" : qUnion([Q0])});
            skLineSegment(sketch, "E79", {"start": v(-14.96, 102.73) * mm, "end": v(-27.7, 90) * mm});
            skCircle(sketch, "E80", {"center": v(0.04, 114.73) * mm, "radius": 6 * mm});
            skArc(sketch, "E81", {"start": v(-14.96, 114.73) * mm, "mid": v(0.04, 129.73) * mm, "end": v(15.04, 114.73) * mm});
            skLineSegment(sketch, "E82", {"start": v(15.04, 114.73) * mm, "end": v(15.04, 102.73) * mm});
            skLineSegment(sketch, "E83", {"start": v(15.04, 102.73) * mm, "end": v(27.76, 90) * mm});
            skLineSegment(sketch, "E84", {"start": v(0.04, 114.73) * mm, "end": v(0.04, 56.25) * mm, "construction": true});
            skLineSegment(sketch, "E85", {"start": v(-74.89, 0) * mm, "end": v(74.89, 0) * mm, "construction": true});
            skLineSegment(sketch, "E86.MirrorCS", {"start": v(-14.96, -102.73) * mm, "end": v(-27.7, -90) * mm});
            skLineSegment(sketch, "E87.MirrorCS", {"start": v(-14.96, -114.73) * mm, "end": v(-14.96, -69.32) * mm});
            skArc(sketch, "E88.MirrorCS", {"start": v(-14.96, -114.73) * mm, "mid": v(0.04, -129.73) * mm, "end": v(15.04, -114.73) * mm});
            skLineSegment(sketch, "E89.MirrorCS", {"start": v(15.04, -114.73) * mm, "end": v(15.04, -102.73) * mm});
            skLineSegment(sketch, "E90.MirrorCS", {"start": v(15.04, -102.73) * mm, "end": v(27.76, -90) * mm});
            skLineSegment(sketch, "E91.MirrorCS", {"start": v(0.04, -114.73) * mm, "end": v(0.04, -56.25) * mm, "construction": true});
            skCircle(sketch, "E92.MirrorC", {"center": v(0.04, -114.73) * mm, "radius": 6 * mm});
            skLineSegment(sketch, "E93", {"start": v(-27.7, 90) * mm, "end": v(27.76, 90) * mm});
            skLineSegment(sketch, "E94", {"start": v(-27.7, -90) * mm, "end": v(27.76, -90) * mm});
            skLineSegment(sketch, "E95", {"start": v(-14.96, 114.73) * mm, "end": v(-14.96, 102.73) * mm});
            skLineSegment(sketch, "E96.MirrorCS", {"start": v(-14.96, -114.73) * mm, "end": v(-14.96, -102.73) * mm});
            skArc(sketch, "E97", {"start": v(58.8, 46.55) * mm, "mid": v(-0.61, 67.6) * mm, "end": v(-59.29, 44.59) * mm});
            skArc(sketch, "E98", {"start": v(-59.29, -45.08) * mm, "mid": v(-0.1, -67.65) * mm, "end": v(59.29, -45.57) * mm});
            skLineSegment(sketch, "E99", {"start": v(-59.29, 44.59) * mm, "end": v(-59.29, -45.08) * mm});
            skLineSegment(sketch, "E100", {"start": v(58.8, 46.55) * mm, "end": v(59.29, -45.57) * mm});
            skSolve(sketch);
        }
        {
            var Q0;
            Q0=makeQuery(id+"F16.imprint","IMPRINT",FACE,{"disambiguationData":[TD([[makeQuery(id+"F16.imprint","IMPRINT",EDGE,{"derivedFrom":sQuery(id+"F16.wireOp",EDGE,"E79")}),1.0]])]});
            var Q1;
            {var subQ0=sQuery(id+"F0.wireOp",EDGE,"E22.filletArc");var subQ1=sQuery(id+"F0.wireOp",EDGE,"E7");var subQ2=sQuery(id+"F0.wireOp",EDGE,"E6");var subQ3=sQuery(id+"F0.wireOp",EDGE,"E5");var subQ4=sQuery(id+"F0.wireOp",EDGE,"E4");var subQ5=sQuery(id+"F0.wireOp",EDGE,"E1.bottom");var subQ6=sQuery(id+"F0.wireOp",EDGE,"E21.filletArc");var subQ7=sQuery(id+"F0.wireOp",EDGE,"E1.top");var subQ8=sQuery(id+"F0.wireOp",EDGE,"E1.left");var subQ9=sQuery(id+"F0.wireOp",EDGE,"E1.right");var subQ10=sQuery(id+"F0.wireOp",EDGE,"E23.filletArc");var subQ11=sQuery(id+"F0.wireOp",EDGE,"E24.filletArc");Q1=makeQuery(id+"F2.boolean.opBoolean","SPLIT",FACE,{"disambiguationData":[TD([makeQuery(id+"F1.opExtrude","SWEPT_FACE",FACE,{"disambiguationData":[OSD([subQ5])]})])],"derivedFrom":makeQuery(id+"F1.opExtrude","CAP_FACE",FACE,{"disambiguationData":[OSD([subQ5,subQ7,subQ8,subQ9,subQ4,subQ3,subQ2,subQ1,subQ6,subQ0,subQ10,subQ11])],"isStart":true})});}
            var Q2;
            {var subQ4=sQuery(id+"F16.wireOp",EDGE,"E96.MirrorCS");Q2=makeQuery(id+"F16.imprint","IMPRINT",FACE,{"disambiguationData":[TD([[makeQuery(id+"F16.imprint","IMPRINT",EDGE,{"derivedFrom":subQ4}),-1.0]])]});}
            var Q3;
            {var subQ0=sQuery(id+"F16.wireOp",EDGE,"E86.MirrorCS");Q3=makeQuery(id+"F16.imprint","IMPRINT",FACE,{"disambiguationData":[TD([[makeQuery(id+"F16.imprint","IMPRINT",EDGE,{"derivedFrom":subQ0}),-1.0]])]});}
            var Q4;
            Q4=makeQuery(id+"F2.opExtrude","CAP_FACE",FACE,{"disambiguationData":[OSD([sQuery(id+"F0.wireOp",EDGE,"E12"),sQuery(id+"F0.wireOp",EDGE,"E13"),sQuery(id+"F0.wireOp",EDGE,"E14"),sQuery(id+"F0.wireOp",EDGE,"E15"),sQuery(id+"F0.wireOp",EDGE,"E17.filletArc"),sQuery(id+"F0.wireOp",EDGE,"E18.filletArc"),sQuery(id+"F0.wireOp",EDGE,"E19.filletArc"),sQuery(id+"F0.wireOp",EDGE,"E20.filletArc"),sQuery(id+"F0.wireOp",EDGE,"E25.0"),sQuery(id+"F0.wireOp",EDGE,"E25.1"),sQuery(id+"F0.wireOp",EDGE,"E25.2"),sQuery(id+"F0.wireOp",EDGE,"E25.3"),sQuery(id+"F0.wireOp",EDGE,"E25.4"),sQuery(id+"F0.wireOp",EDGE,"E25.5"),sQuery(id+"F0.wireOp",EDGE,"E25.6"),sQuery(id+"F0.wireOp",EDGE,"E25.7")])],"isStart":false});
            extrude(context, id + "F17", {"entities" : qUnion([Q0, Q1, Q2, Q3]), "endBound" : BoundingType.UP_TO_SURFACE, "endBoundEntityFace" : qUnion([Q4]), "depth" : 5.7 * mm});
        }
    });
